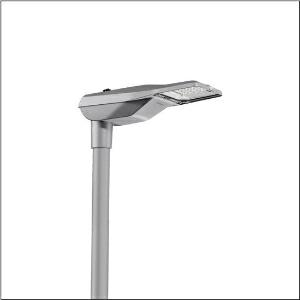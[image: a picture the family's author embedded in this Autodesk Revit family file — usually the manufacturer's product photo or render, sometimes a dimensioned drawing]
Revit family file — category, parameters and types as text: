
# Revit family: streetlight_sl_21_micro___st1_0a_5xe1d33s08db_38a0
name_source: partatom
category: Lighting Fixtures
units: mm (PartAtom-declared; Revit-internal decimal feet)

## family parameters
Cut with Voids When Loaded = No
Host = Face
Light Source = No
Part Type = Normal
Room Calculation Point = No
Round Connector Dimension = Use Diameter
Shared = No

## types (1)
- --- (1 x LED, 5110 lm, 39.1 W, 3000K)
    Apparent Load = 39 VA
    CIE Flux Codes = 37 72 97 100 100
    Color Rendering = 70
    Color Temperature = 3000K
    Default Elevation = 1800 mm
    Description = Streetlight SL 21 micro, mast luminaire, primary light control with lens, of PMMA, primary optical cover: cover, of toughened safety glass, transparent, light distribution: ST1.0a, light emission: direct distribution, primary light characteristic: asymmetric, installation type: side-entry, post-top, LED, High Power LED, rated luminous flux: 5.110lm, luminous efficacy: 131lm/W, light colour: 730, colour temperature: 3000K, control: flexible luminous flux parameterisation, time-dependent luminous flux control, constant luminous flux control, overheat protection, presetting dimming logarithmic, mains connection: 220..240V, AC, 50/60Hz, start of lifetime: 39W, end of service life: 41W, reduction: 18W, luminaire housing, of diecast aluminium, powder-coated, Siteco® metallic grey (DB 702S), corrosivity category C5 mid according to DIN EN ISO 12944, please order mast flange separately, inclination adjustable: 0°, 5°, 10°, 15°, sealing non-destructively replaceable, multi-level sealing system, length: 528mm, width: 235mm, height: 110mm, mast flange for spigot size: 42mm (side-entry): 5XC10008XM4, 60/48mm (side-entry/post-top): 5XC10108XM2, 76/60mm (side-entry/post-top): 5XC10108XM1, Smart Interface above, protection rating (complete): IP66, insulation class (complete): insulation class II (safety insulation), certification: CE, ENEC, ENEC+, VDE, impact resistance: IK09, permissible operating ambient temperature for outdoor applications: -40..+50°C, standard-compliant lighting for roads and squares, packaging unit: 1 piece

Light Distribution: ST1.0a
    Height = 110 mm
    Lamp = 1 x LED
    Lamp Light Flux = 5110 lm
    Lamp Power = 39.1 W
    Lamp count = 1
    Length = 528 mm
    Luminous efficacy = 131 lm/W
    Manufacturer = Siteco
    ModVariant = No
    Model = 5XE1D33S08DB
    Number of Poles = 1
    OnlyDefault = Yes
    Power Factor = 1
    Product Name = Streetlight SL 21 micro | ST1.0a
    Product group = mast luminaire | pylon top
    ProductGroupID = 6100
    Protection Class = Protection class II
    Protection Degree = IP 66
    RLX_Detail_Level = 1
    RLX_Emergency_Light_Flux = 0 lm
    RLX_Emergency_Type = 0
    RLX_Emergency_Type_DB = No
    RlxData = <blob elided: 98893 chars, md5=089f00a3>
    Socket = socket
    Standby Power = 0 W
    System Light Flux = 5110 lm
    System Power = 39 W
    Type Comments = factory setting: luminous flux: 100 % | dim-lin: 254 | 765 mA
    Type Image = l_1277292.jpg
    URL = http://relux.com
    VarID = @adj_105991
    Voltage = 0 V
    Weight = 0.00 kg
    Width = 235 mm

## geometry (parser evidence)
native form markers: Blend x4, Sweep x9
no freeform markers — native parametric forms only
